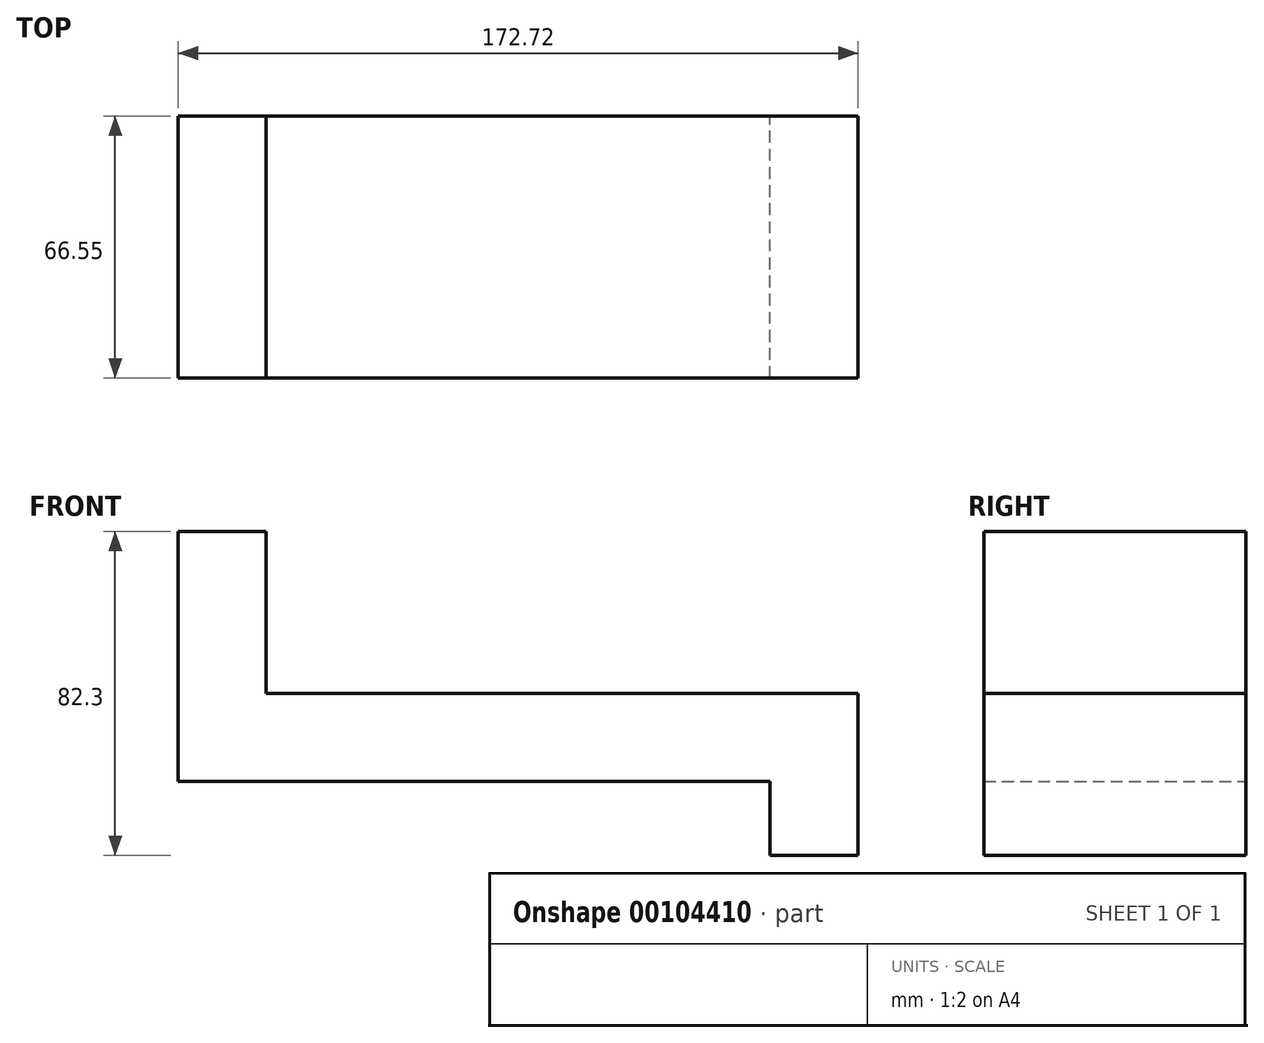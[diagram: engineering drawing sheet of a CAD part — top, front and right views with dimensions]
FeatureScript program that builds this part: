
annotation { "Feature Type Name" : "Feature", "Feature Type Description" : "" }
export const myFeature = defineFeature(function(context is Context, id is Id, definition is map)
    precondition{}
    {
        {
            var Q0;
            Q0=qCreatedBy(makeId("Top.planeOp"),FACE);
            var sketch = newSketch(context, id + "F0", { "sketchPlane" : qUnion([Q0])});
            skLineSegment(sketch, "E0.bottom", {"start": v(-85.28, 11.58) * mm, "end": v(87.44, 11.58) * mm});
            skLineSegment(sketch, "E0.top", {"start": v(-85.28, -54.97) * mm, "end": v(87.44, -54.97) * mm});
            skLineSegment(sketch, "E0.left", {"start": v(-85.28, 11.58) * mm, "end": v(-85.28, -54.97) * mm});
            skLineSegment(sketch, "E0.right", {"start": v(87.44, 11.58) * mm, "end": v(87.44, -54.97) * mm});
            skSolve(sketch);
        }
        {
            var Q0;
            Q0 = qSketchRegion(id + "F0", true);
            extrude(context, id + "F1", {"entities" : qUnion([Q0]), "depth" : 22.35 * mm});
        }
        {
            var Q0;
            Q0=makeQuery(id+"F1.opExtrude","CAP_FACE",FACE,{"disambiguationData":[OSD([sQuery(id+"F0.wireOp",EDGE,"E0.bottom"),sQuery(id+"F0.wireOp",EDGE,"E0.top"),sQuery(id+"F0.wireOp",EDGE,"E0.left"),sQuery(id+"F0.wireOp",EDGE,"E0.right")])],"isStart":false});
            var sketch = newSketch(context, id + "F2", { "sketchPlane" : qUnion([Q0])});
            skLineSegment(sketch, "E1.bottom", {"start": v(-85.28, 11.58) * mm, "end": v(-62.93, 11.58) * mm});
            skLineSegment(sketch, "E1.top", {"start": v(-85.28, -54.97) * mm, "end": v(-62.93, -54.97) * mm});
            skLineSegment(sketch, "E1.left", {"start": v(-85.28, 11.58) * mm, "end": v(-85.28, -54.97) * mm});
            skLineSegment(sketch, "E1.right", {"start": v(-62.93, 11.58) * mm, "end": v(-62.93, -54.97) * mm});
            skSolve(sketch);
        }
        {
            var Q0;
            Q0 = qSketchRegion(id + "F2", true);
            extrude(context, id + "F3", {"entities" : qUnion([Q0]), "operationType" : NewBodyOperationType.ADD, "depth" : 41.15 * mm});
        }
        {
            var Q0;
            Q0=makeQuery(id+"F1.opExtrude","CAP_FACE",FACE,{"disambiguationData":[OSD([sQuery(id+"F0.wireOp",EDGE,"E0.bottom"),sQuery(id+"F0.wireOp",EDGE,"E0.top"),sQuery(id+"F0.wireOp",EDGE,"E0.left"),sQuery(id+"F0.wireOp",EDGE,"E0.right")])],"isStart":true});
            var sketch = newSketch(context, id + "F4", { "sketchPlane" : qUnion([Q0])});
            skLineSegment(sketch, "E2.bottom", {"start": v(87.44, 54.97) * mm, "end": v(65.09, 54.97) * mm});
            skLineSegment(sketch, "E2.top", {"start": v(87.44, -11.58) * mm, "end": v(65.09, -11.58) * mm});
            skLineSegment(sketch, "E2.left", {"start": v(87.44, 54.97) * mm, "end": v(87.44, -11.58) * mm});
            skLineSegment(sketch, "E2.right", {"start": v(65.09, 54.97) * mm, "end": v(65.09, -11.58) * mm});
            skSolve(sketch);
        }
        {
            var Q0;
            Q0 = qSketchRegion(id + "F4", true);
            extrude(context, id + "F5", {"entities" : qUnion([Q0]), "operationType" : NewBodyOperationType.ADD, "depth" : 18.8 * mm});
        }
    });
